# Revit family: Shower-Shower_Arm-KOHLER-K-26322T_1
name_source: partatom
category: Plumbing Fixtures
revit_build: Autodesk Revit 2017 (Build: 20160225_1515(x64)
units: mm (PartAtom-declared; Revit-internal decimal feet)

## family parameters
Cut with Voids When Loaded = No
Host = Face
OmniClass Number = 23.31.17.00
OmniClass Title = Showers
Part Type = Normal
Room Calculation Point = No
Round Connector Dimension = Use Diameter
Shared = No

## types (1)
- Not a Type-See Type Catalog
    ADA Compliant = No
    Assembly Code = D2010700
    CW Connection = No
    Cold Water Inlet = Cold Water Inlet
    Date Modified = 02/09/2021
    Default Elevation = 72"
    Description = Wall mount right angle I-Function
    Drain Included = No
    Finish = Default
    Flow Rate = 0 GPM
    HW Connection = Yes
    Height = 2 3/16"
    Hot Water Inlet = Tempered Water Inlet
    Length = 13 5/8"
    Manufacturer = KOHLER Co.
    Master Format 2014 = 22 42 23
    Master Format 2014 Name = Residential Showers
    Material = Brass Construction
    Pressure = 0.00 psi
    Type = 0
    URL = http://www.kohler.com.cn
    Vent Connection = No
    Waste Connection = No
    Waste Water Outlet = Waste Water Outlet
    WaterSense Certified = No
    Width = 2 3/16"

## geometry (parser evidence)
native form markers: Sweep x6
no freeform markers — native parametric forms only
